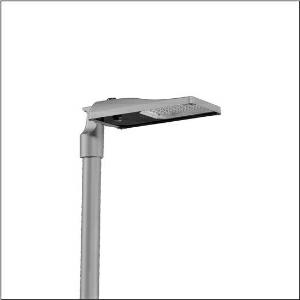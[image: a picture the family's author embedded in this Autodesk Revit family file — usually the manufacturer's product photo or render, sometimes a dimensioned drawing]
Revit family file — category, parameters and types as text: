
# Revit family: streetlight_sl_31_mini___st1_0a_5xh2d71t08ja_f6e8
name_source: partatom
category: Lighting Fixtures
units: mm (PartAtom-declared; Revit-internal decimal feet)

## family parameters
Cut with Voids When Loaded = No
Host = Face
Light Source = No
Part Type = Normal
Room Calculation Point = No
Round Connector Dimension = Use Diameter
Shared = No

## types (1)
- --- (1 x LED, 9900 lm, 82.5 W, 2200K)
    Apparent Load = 83 VA
    CIE Flux Codes = 40 73 97 100 100
    Color Rendering = 70
    Color Temperature = 2200K
    Default Elevation = 1800 mm
    Description = Streetlight SL 31 mini D4i, Desk-Remote mast luminaire for post-top, side-entry; light control with lens of PMMA; light distribution: ST1.0a, direct asymmetric distribution, for standard-compliant lighting for roads and squares; LED: luminous flux: 9.900lm, light colour: 722, colour temperature: 2200K; luminous efficacy: 120lm/W; control: pre-setting: logarithmic dimming characteristic, flexible luminous flux parameterisation, time-dependent luminous flux control, constant luminous flux control, power reduction, intelligent temperature release in ECG and LED module, overheat protection; luminaire housing, of diecast aluminium, Siteco® metallic grey (DB 702S), corrosivity category C5 high according to DIN EN ISO 12944; cover of toughened safety glass, transparent, mast flange of diecast aluminium, Siteco® metallic grey (DB 702S), spigot size: 76/60mm, mast flange included unmounted; with cable H07RN-F 2x 1.5mm², cable length: 10,5m, connection cable pre-assembled; mains connection: 220..240V, AC, 50/60Hz; power consumption (at start of service life): 82,5W / (at end of service life): 90,1W / (with reduced operation 50%): 36,5W; protection rating (complete): IP66; insulation class (complete): insulation class II (safety insulation); impact resistance: IK09; certification: CE, ENEC, ENEC+, VDE, UKCA, ZD4i; permissible operating ambient temperature for outdoor applications: -40..+50°C; packaging unit: 1 piece

Light Distribution: ST1.0a
    Height = 76 mm
    Lamp = 1 x LED
    Lamp Light Flux = 9900 lm
    Lamp Power = 82.5 W
    Lamp count = 1
    Length = 547 mm
    Luminous efficacy = 120 lm/W
    Manufacturer = Siteco
    ModVariant = No
    Model = 5XH2D71T08JA
    Number of Poles = 1
    OnlyDefault = Yes
    Power Factor = 1
    Product Name = Streetlight SL 31 mini | ST1.0a
    Product group = mast luminaire | pylon top
    ProductGroupID = 6100
    Protection Class = Protection class II
    Protection Degree = IP 66
    RLX_Detail_Level = 1
    RLX_Emergency_Light_Flux = 0 lm
    RLX_Emergency_Type = 0
    RLX_Emergency_Type_DB = No
    RlxData = <blob elided: 39805 chars, md5=eb78dac4>
    Socket = socket
    Standby Power = 0 W
    System Light Flux = 9900 lm
    System Power = 83 W
    Type Comments = factory setting: luminous flux: 100 % | dim-lin: 254 | 870 mA
    Type Image = l_1300332.jpg
    URL = http://relux.com
    VarID = @adj_008549
    Voltage = 0 V
    Weight = 0.00 kg
    Width = 265 mm

## geometry (parser evidence)
native form markers: Blend x4, Sweep x11
no freeform markers — native parametric forms only
